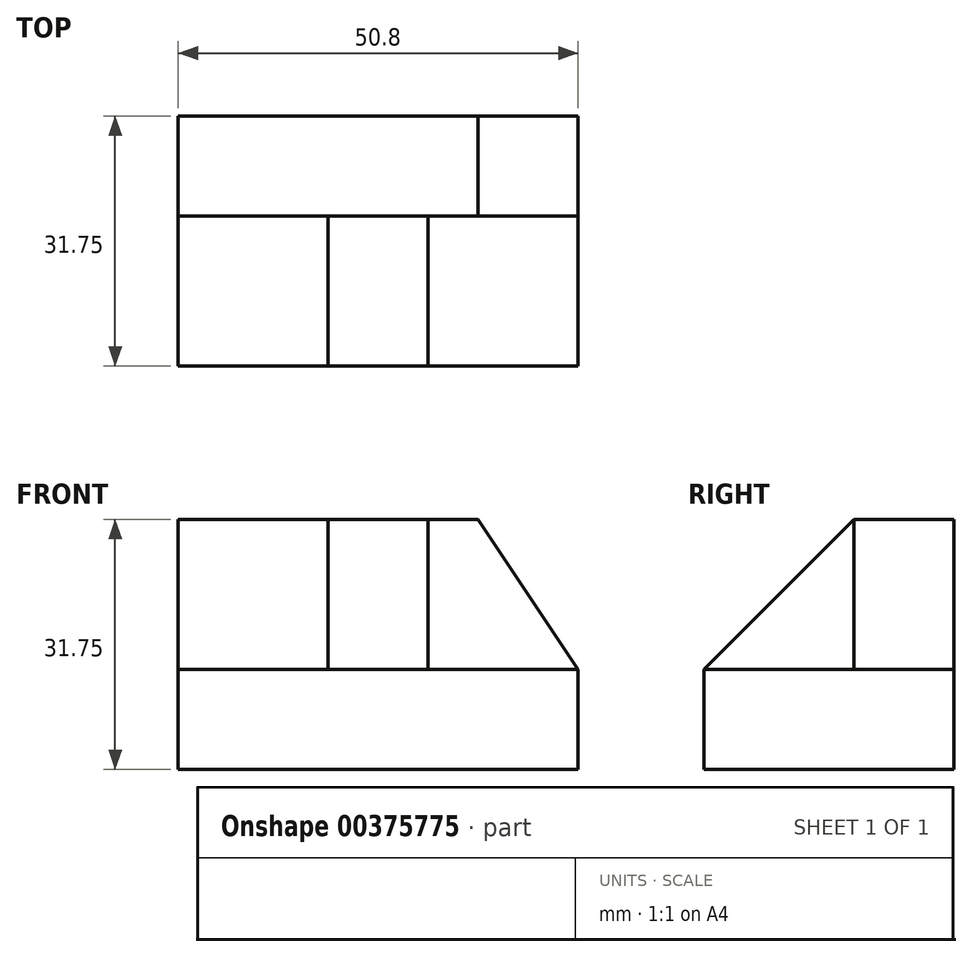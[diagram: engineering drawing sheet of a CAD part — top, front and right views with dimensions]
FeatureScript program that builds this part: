
annotation { "Feature Type Name" : "Feature", "Feature Type Description" : "" }
export const myFeature = defineFeature(function(context is Context, id is Id, definition is map)
    precondition{}
    {
        {
            var Q0;
            Q0=qCreatedBy(makeId("Front.planeOp"),FACE);
            var sketch = newSketch(context, id + "F0", { "sketchPlane" : qUnion([Q0])});
            skLineSegment(sketch, "E0", {"start": v(0, 0) * mm, "end": v(50.8, 0) * mm});
            skLineSegment(sketch, "E1", {"start": v(50.8, 0) * mm, "end": v(50.8, 31.75) * mm});
            skLineSegment(sketch, "E2", {"start": v(50.8, 31.75) * mm, "end": v(0, 31.75) * mm});
            skLineSegment(sketch, "E3", {"start": v(0, 31.75) * mm, "end": v(0, 0) * mm});
            skSolve(sketch);
        }
        {
            var Q0;
            Q0 = qSketchRegion(id + "F0", true);
            extrude(context, id + "F1", {"entities" : qUnion([Q0]), "depth" : 31.75 * mm});
        }
        {
            var Q0;
            Q0=makeQuery(id+"F1.opExtrude","CAP_FACE",FACE,{"disambiguationData":[OSD([sQuery(id+"F0.wireOp",EDGE,"E0"),sQuery(id+"F0.wireOp",EDGE,"E1"),sQuery(id+"F0.wireOp",EDGE,"E2"),sQuery(id+"F0.wireOp",EDGE,"E3")])],"isStart":false});
            var sketch = newSketch(context, id + "F2", { "sketchPlane" : qUnion([Q0])});
            skLineSegment(sketch, "E4", {"start": v(0, 12.7) * mm, "end": v(19.05, 12.7) * mm});
            skLineSegment(sketch, "E5", {"start": v(19.05, 12.7) * mm, "end": v(19.05, 31.75) * mm});
            skLineSegment(sketch, "E6", {"start": v(31.75, 31.75) * mm, "end": v(31.75, 12.7) * mm});
            skLineSegment(sketch, "E7", {"start": v(31.75, 12.7) * mm, "end": v(50.8, 12.7) * mm});
            skSolve(sketch);
        }
        {
            var Q0;
            {var subQ0=sQuery(id+"F2.wireOp",EDGE,"E4");Q0=makeQuery(id+"F2.imprint","IMPRINT",FACE,{"disambiguationData":[TD([[makeQuery(id+"F2.imprint","IMPRINT",EDGE,{"derivedFrom":subQ0}),1.0]])]});}
            var Q1;
            {var subQ0=sQuery(id+"F2.wireOp",EDGE,"E6");Q1=makeQuery(id+"F2.imprint","IMPRINT",FACE,{"disambiguationData":[TD([[makeQuery(id+"F2.imprint","IMPRINT",EDGE,{"derivedFrom":subQ0}),1.0]])]});}
            extrude(context, id + "F3", {"entities" : qUnion([Q0, Q1]), "operationType" : NewBodyOperationType.REMOVE, "oppositeDirection" : true, "depth" : 19.05 * mm});
        }
        {
            var Q0;
            Q0=makeQuery(id+"F3.boolean.opBoolean","COPY",FACE,{"derivedFrom":makeQuery(id+"F3.opExtrude","CAP_FACE",FACE,{"disambiguationData":[OSD([sQuery(id+"F0.wireOp",EDGE,"E1"),sQuery(id+"F0.wireOp",EDGE,"E2"),sQuery(id+"F2.wireOp",EDGE,"E6"),sQuery(id+"F2.wireOp",EDGE,"E7")])],"isStart":false})});
            var sketch = newSketch(context, id + "F4", { "sketchPlane" : qUnion([Q0])});
            skLineSegment(sketch, "E8", {"start": v(38.1, 31.75) * mm, "end": v(50.8, 12.7) * mm});
            skSolve(sketch);
        }
        {
            var Q0;
            {var subQ0=sQuery(id+"F4.wireOp",EDGE,"E8");Q0=makeQuery(id+"F4.imprint","IMPRINT",FACE,{"disambiguationData":[TD([[makeQuery(id+"F4.imprint","IMPRINT",EDGE,{"derivedFrom":subQ0}),1.0]])]});}
            extrude(context, id + "F5", {"entities" : qUnion([Q0]), "operationType" : NewBodyOperationType.REMOVE, "oppositeDirection" : true, "depth" : 25.4 * mm});
        }
        {
            var Q0;
            Q0=makeQuery(id+"F3.boolean.opBoolean","COPY",FACE,{"derivedFrom":makeQuery(id+"F3.opExtrude","SWEPT_FACE",FACE,{"disambiguationData":[OSD([sQuery(id+"F2.wireOp",EDGE,"E6")])]})});
            var sketch = newSketch(context, id + "F6", { "sketchPlane" : qUnion([Q0])});
            skLineSegment(sketch, "E9", {"start": v(-12.7, 31.75) * mm, "end": v(-31.75, 12.7) * mm});
            skSolve(sketch);
        }
        {
            var Q0;
            Q0=makeQuery(id+"F6.imprint","IMPRINT",FACE,{"disambiguationData":[TD([[makeQuery(id+"F6.imprint","IMPRINT",EDGE,{"derivedFrom":sQuery(id+"F6.wireOp",EDGE,"E9")}),-1.0]])]});
            extrude(context, id + "F7", {"entities" : qUnion([Q0]), "operationType" : NewBodyOperationType.REMOVE, "oppositeDirection" : true, "depth" : 25.4 * mm});
        }
    });
